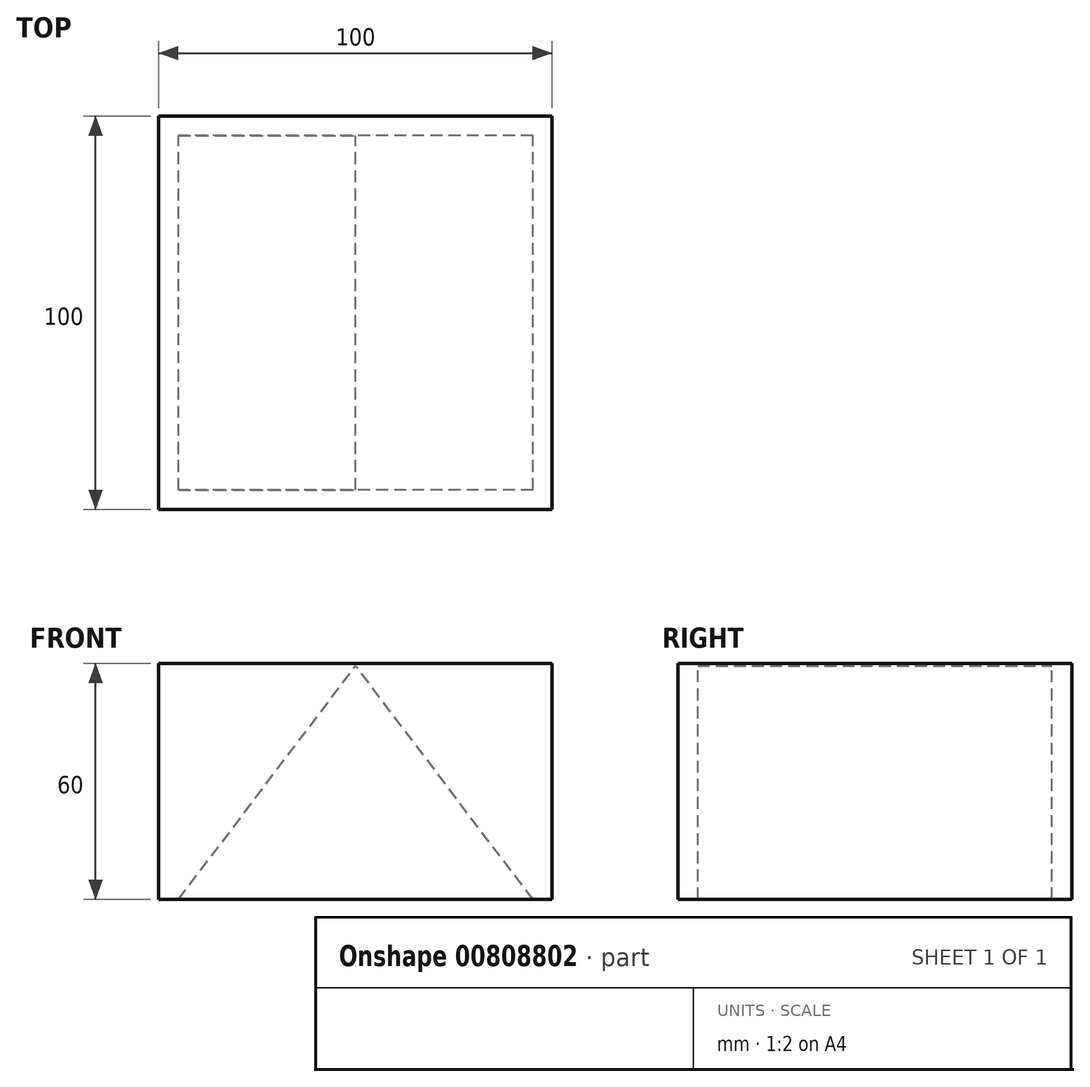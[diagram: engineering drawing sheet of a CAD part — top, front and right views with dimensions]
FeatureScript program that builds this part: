
annotation { "Feature Type Name" : "Feature", "Feature Type Description" : "" }
export const myFeature = defineFeature(function(context is Context, id is Id, definition is map)
    precondition{}
    {
        {
            var Q0;
            Q0=qCreatedBy(makeId("Top.planeOp"),FACE);
            var sketch = newSketch(context, id + "F0", { "sketchPlane" : qUnion([Q0])});
            skLineSegment(sketch, "E0.bottom", {"start": v(0, 0) * mm, "end": v(-100, 0) * mm});
            skLineSegment(sketch, "E0.top", {"start": v(0, 100) * mm, "end": v(-100, 100) * mm});
            skLineSegment(sketch, "E0.left", {"start": v(0, 0) * mm, "end": v(0, 100) * mm});
            skLineSegment(sketch, "E0.right", {"start": v(-100, 0) * mm, "end": v(-100, 100) * mm});
            skSolve(sketch);
        }
        {
            var Q0;
            Q0=makeQuery(id+"F0.imprint","IMPRINT",FACE,{"disambiguationData":[TD([[makeQuery(id+"F0.imprint","IMPRINT",EDGE,{"derivedFrom":sQuery(id+"F0.wireOp",EDGE,"E0.bottom")}),-1.0]])]});
            extrude(context, id + "F1", {"entities" : qUnion([Q0]), "depth" : 60 * mm, "offsetDistance" : 25.4 * mm});
        }
        {
            var Q0;
            Q0=makeQuery(id+"F1.opExtrude","SWEPT_FACE",FACE,{"disambiguationData":[OSD([sQuery(id+"F0.wireOp",EDGE,"E0.top")])]});
            cPlane(context, id + "F2", {"entities" : qUnion([Q0]), "cplaneType" : CPlaneType.OFFSET, "offset" : 5 * mm, "oppositeDirection" : true, "width" : 152.4 * mm, "height" : 152.4 * mm});
        }
        {
            var Q0;
            Q0=makeQuery(id+"F1.opExtrude","SWEPT_FACE",FACE,{"disambiguationData":[OSD([sQuery(id+"F0.wireOp",EDGE,"E0.left")])]});
            cPlane(context, id + "F3", {"entities" : qUnion([Q0]), "cplaneType" : CPlaneType.OFFSET, "offset" : 5 * mm, "oppositeDirection" : true, "width" : 152.4 * mm, "height" : 152.4 * mm});
        }
        {
            var Q0;
            Q0=qCreatedBy(id+"F2.planeOp",FACE);
            var sketch = newSketch(context, id + "F4", { "sketchPlane" : qUnion([Q0])});
            skLineSegment(sketch, "E1", {"start": v(4.9, 0) * mm, "end": v(49.9, 59.36) * mm});
            skLineSegment(sketch, "E2", {"start": v(4.9, 0) * mm, "end": v(4.9, 60) * mm, "construction": true});
            skLineSegment(sketch, "E3", {"start": v(4.9, 60) * mm, "end": v(49.9, 59.36) * mm, "construction": true});
            skLineSegment(sketch, "E4", {"start": v(49.9, 59.36) * mm, "end": v(49.9, 0) * mm, "construction": true});
            skLineSegment(sketch, "E5.MirrorCS", {"start": v(94.9, 0) * mm, "end": v(49.9, 59.36) * mm});
            skLineSegment(sketch, "E6", {"start": v(4.9, 0) * mm, "end": v(94.9, 0) * mm});
            skSolve(sketch);
        }
        {
            var Q0;
            Q0 = qSketchRegion(id + "F4", true);
            extrude(context, id + "F5", {"entities" : qUnion([Q0]), "operationType" : NewBodyOperationType.REMOVE, "oppositeDirection" : true, "depth" : 90 * mm, "offsetDistance" : 25.4 * mm});
        }
    });
